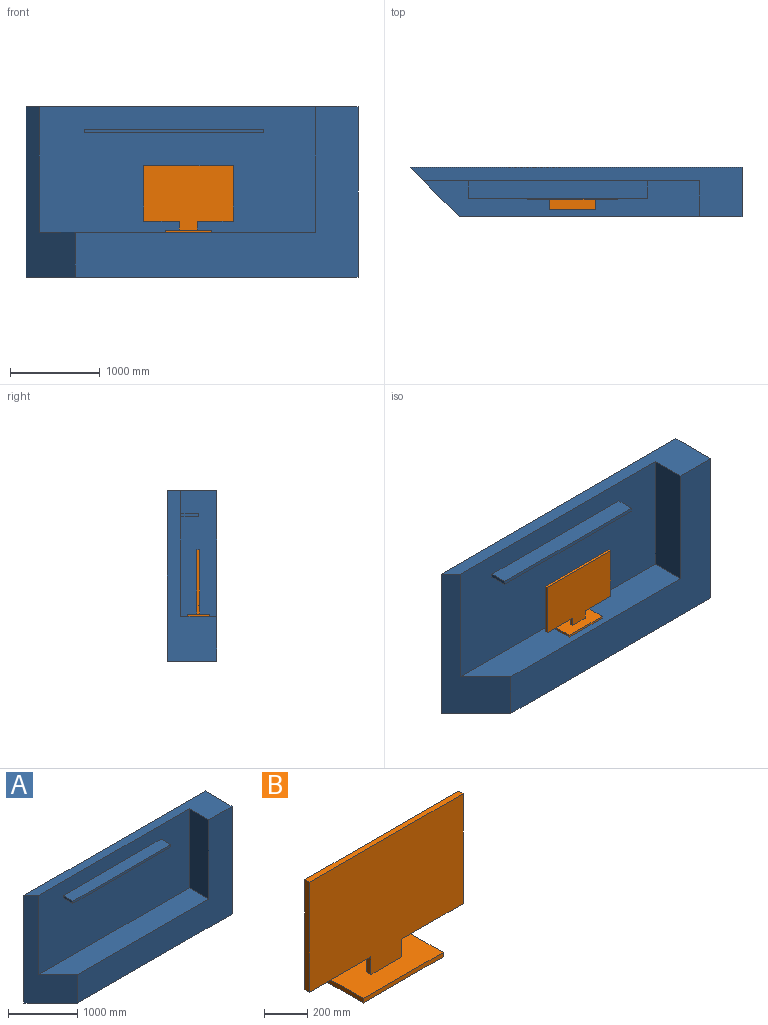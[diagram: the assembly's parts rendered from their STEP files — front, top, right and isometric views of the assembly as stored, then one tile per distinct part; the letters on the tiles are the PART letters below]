
ASSEMBLY  parts=2 mates=1
PART A: 14 faces, bbox 3700x550x1900 mm
  f0: plane 3076.03x400mm, normal (0,0,1), area 1150413.2mm2, adj f1,f2,f3,f8
  f1: plane 3076.03x1400mm, normal (0,-1,0), area 4226446.2mm2, adj f0,f2,f7,f8,f9,f10,f11,f12
  f2: plane 1900x550mm, normal (-0.71,-0.71,0), area 685893.6mm2, adj f0,f1,f3,f5,f6,f7
  f3: plane 3150x1900mm, normal (0,-1,0), area 2238553.8mm2, adj f0,f2,f4,f6,f7,f8
  f4: plane 1900x550mm, normal (1,0,0), area 1045000mm2, adj f3,f5,f6,f7
  f5: plane 3700x1900mm, normal (0,1,0), area 7030000mm2, adj f2,f4,f6,f7
  f6: plane 3700x550mm, normal (0,0,-1), area 1883750mm2, adj f2,f3,f4,f5
  f7: plane 3700x550mm, normal (0,0,1), area 733336.8mm2, adj f1,f2,f3,f4,f5,f8
  f8: plane 1400x400mm, normal (-1,0,0), area 560000mm2, adj f0,f1,f3,f7
  f9: plane 2000x200mm, normal (0,0,1), area 400000mm2, adj f1,f10,f12,f13
  f10: plane 200x40mm, normal (-1,0,0), area 8000mm2, adj f1,f9,f11,f13
  f11: plane 2000x200mm, normal (0,0,-1), area 400000mm2, adj f1,f10,f12,f13
  f12: plane 200x40mm, normal (1,0,0), area 8000mm2, adj f1,f9,f11,f13
  f13: plane 2000x40mm, normal (0,-1,0), area 80000mm2, adj f9,f10,f11,f12
PART B: 15 faces, bbox 1000x250x745 mm
  f0: plane 400x30mm, normal (0,0,-1), area 12000mm2, adj f3,f5,f6,f8
  f1: plane 620x30mm, normal (-1,0,0), area 18600mm2, adj f2,f4,f5,f6
  f2: plane 400x30mm, normal (0,0,-1), area 12000mm2, adj f1,f5,f6,f7
  f3: plane 620x30mm, normal (1,0,0), area 18600mm2, adj f0,f4,f5,f6
  f4: plane 1000x30mm, normal (0,0,1), area 30000mm2, adj f1,f3,f5,f6
  f5: plane 1000x720mm, normal (0,1,0), area 640000mm2, adj f0,f1,f2,f3,f4,f7,f8,f14
  f6: plane 1000x720mm, normal (0,-1,0), area 640000mm2, adj f0,f1,f2,f3,f4,f7,f8,f14
  f7: plane 100x30mm, normal (-1,0,0), area 3000mm2, adj f2,f5,f6,f14
  f8: plane 100x30mm, normal (1,0,0), area 3000mm2, adj f0,f5,f6,f14
  f9: plane 250x25mm, normal (-1,0,0), area 6250mm2, adj f10,f12,f13,f14
  f10: plane 520x25mm, normal (0,1,0), area 13000mm2, adj f9,f11,f13,f14
  f11: plane 250x25mm, normal (1,0,0), area 6250mm2, adj f10,f12,f13,f14
  f12: plane 520x25mm, normal (0,-1,0), area 13000mm2, adj f9,f11,f13,f14
  f13: plane 520x250mm, normal (0,0,-1), area 130000mm2, adj f9,f10,f11,f12
  f14: plane 520x250mm, normal (0,0,1), area 124000mm2, adj f5,f6,f7,f8,f9,f10,f11,f12
PLACE A t=(-3150,0,0)mm
PLACE B t=(-2390,190,625)mm
MATE fastened B.f13 <-> A.f0  axis (0,0,-1) through (-2150,80,500)mm
